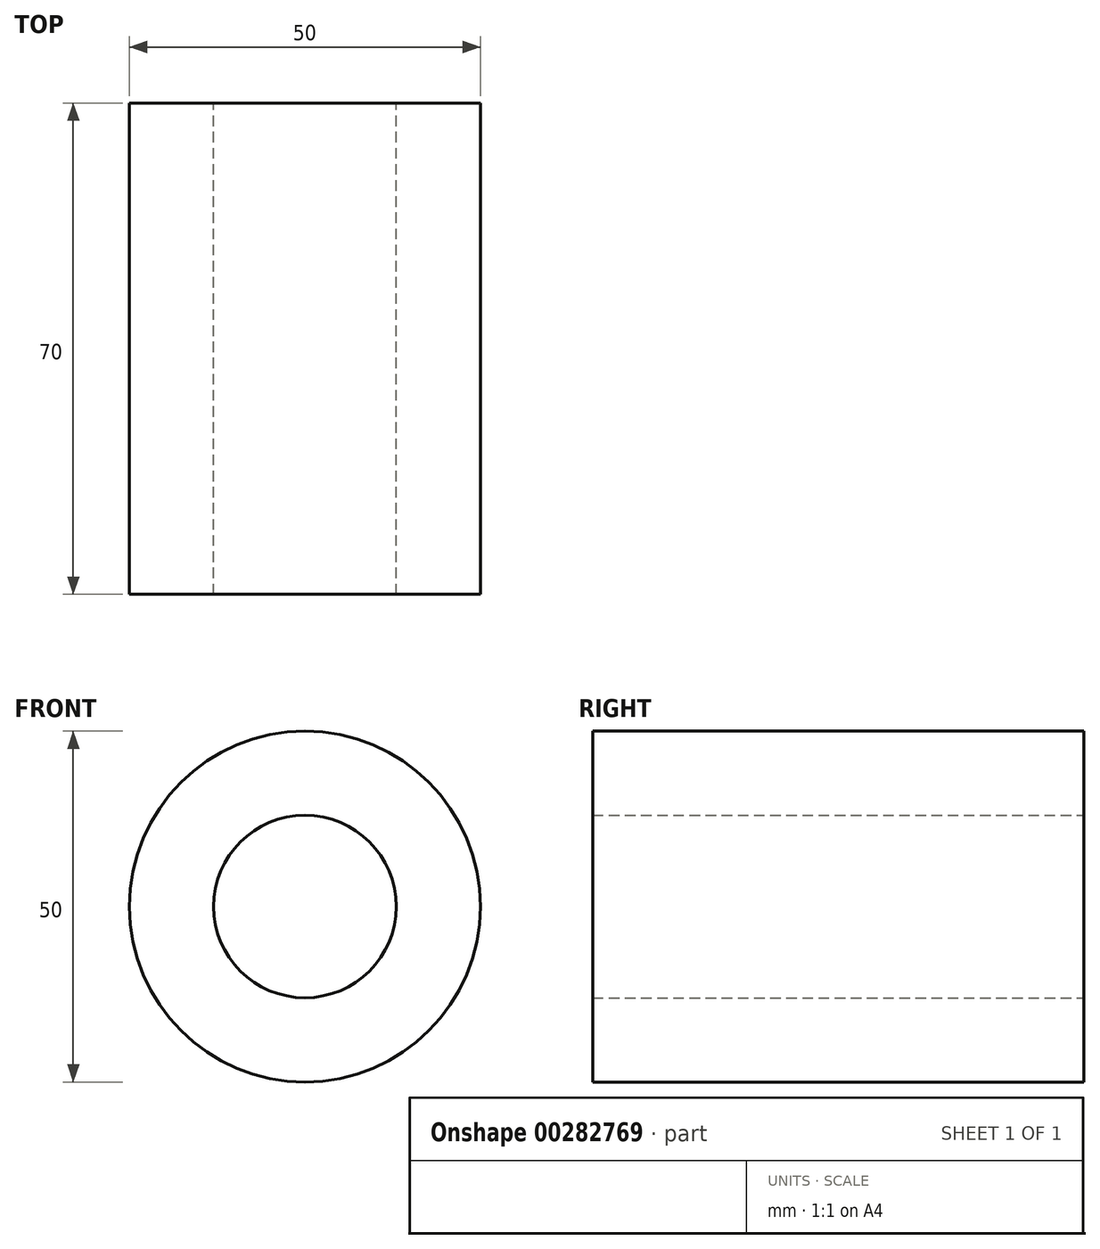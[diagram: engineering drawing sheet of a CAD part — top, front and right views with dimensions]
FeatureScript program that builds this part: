
annotation { "Feature Type Name" : "Feature", "Feature Type Description" : "" }
export const myFeature = defineFeature(function(context is Context, id is Id, definition is map)
    precondition{}
    {
        {
            var Q0;
            Q0=qCreatedBy(makeId("Front.planeOp"),FACE);
            var sketch = newSketch(context, id + "F0", { "sketchPlane" : qUnion([Q0])});
            skCircle(sketch, "E0", {"center": v(0, 0) * mm, "radius": 13 * mm});
            skCircle(sketch, "E1", {"center": v(0, 0) * mm, "radius": 25 * mm});
            skSolve(sketch);
        }
        {
            var Q0;
            Q0=makeQuery(id+"F0.imprint","IMPRINT",FACE,{"disambiguationData":[TD([[makeQuery(id+"F0.imprint","IMPRINT",EDGE,{"derivedFrom":sQuery(id+"F0.wireOp",EDGE,"E0")}),-1.0]])]});
            extrude(context, id + "F1", {"entities" : qUnion([Q0]), "depth" : 70 * mm});
        }
    });
